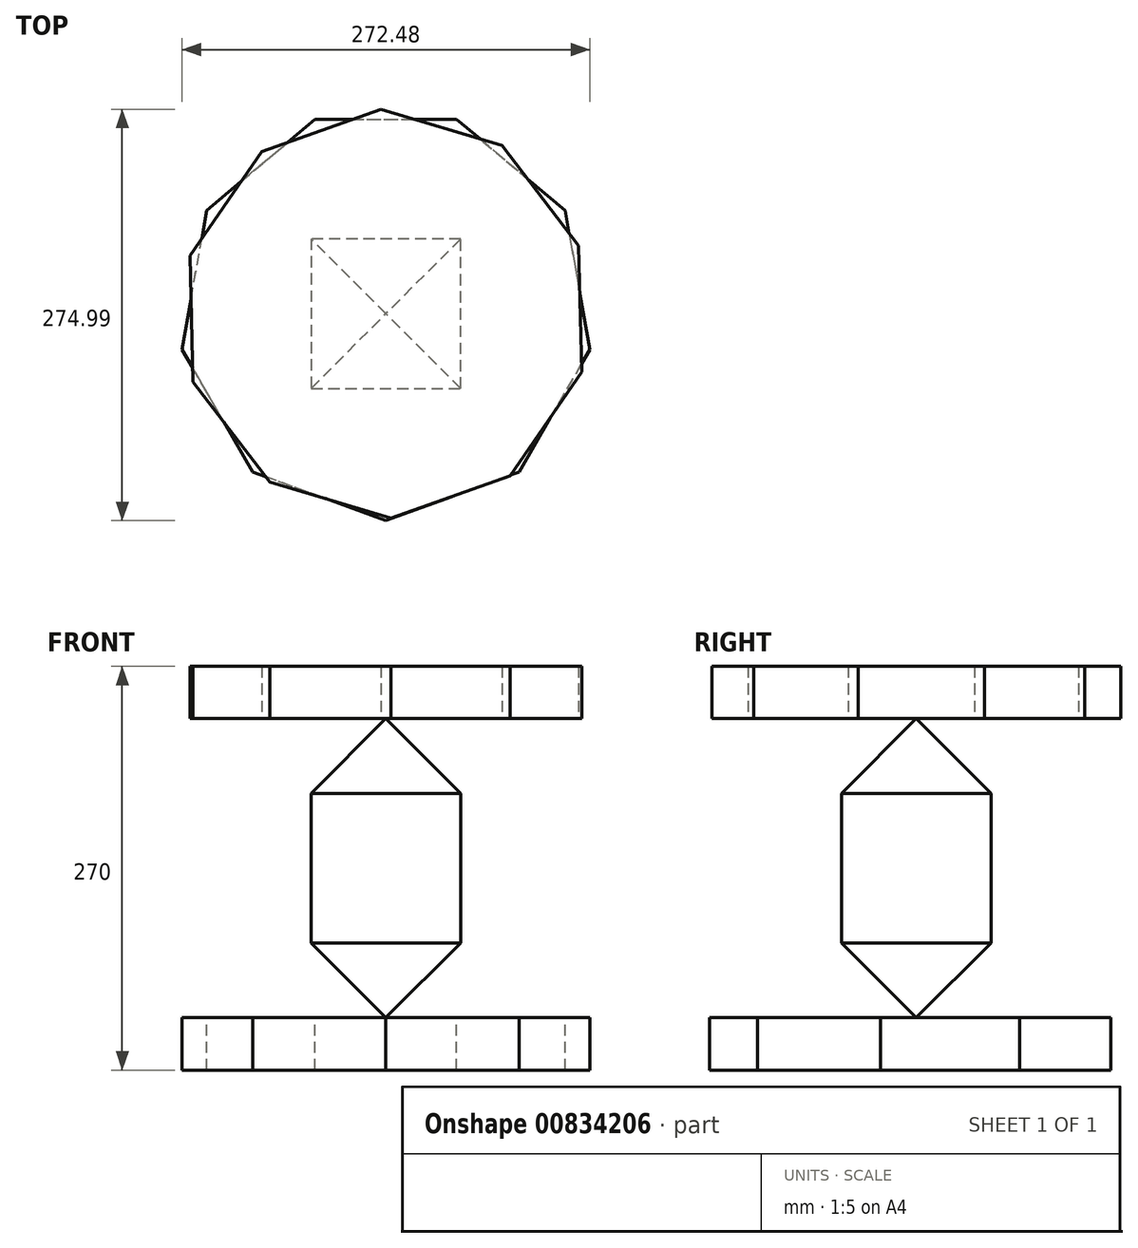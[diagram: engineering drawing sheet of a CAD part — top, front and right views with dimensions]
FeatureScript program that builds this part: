
annotation { "Feature Type Name" : "Feature", "Feature Type Description" : "" }
export const myFeature = defineFeature(function(context is Context, id is Id, definition is map)
    precondition{}
    {
        {
            var Q0;
            Q0=qCreatedBy(makeId("Top.planeOp"),FACE);
            var sketch = newSketch(context, id + "F0", { "sketchPlane" : qUnion([Q0])});
            skLineSegment(sketch, "E0.bottom", {"start": v(-50, 50) * mm, "end": v(50, 50) * mm});
            skLineSegment(sketch, "E0.top", {"start": v(-50, -50) * mm, "end": v(50, -50) * mm});
            skLineSegment(sketch, "E0.left", {"start": v(-50, 50) * mm, "end": v(-50, -50) * mm});
            skLineSegment(sketch, "E0.right", {"start": v(50, 50) * mm, "end": v(50, -50) * mm});
            skPoint(sketch, "E0.middle", {"position": v(0, 0) * mm});
            skSolve(sketch);
        }
        {
            var Q0;
            Q0=makeQuery(id+"F0.imprint","IMPRINT",FACE,{"disambiguationData":[TD([[makeQuery(id+"F0.imprint","IMPRINT",EDGE,{"derivedFrom":sQuery(id+"F0.wireOp",EDGE,"E0.bottom")}),-1.0]])]});
            extrude(context, id + "F1", {"entities" : qUnion([Q0]), "oppositeDirection" : true, "depth" : 100 * mm, "offsetDistance" : 25 * mm});
        }
        {
            var Q0;
            Q0=makeQuery(id+"F1.opExtrude","CAP_FACE",FACE,{"disambiguationData":[OSD([sQuery(id+"F0.wireOp",EDGE,"E0.bottom"),sQuery(id+"F0.wireOp",EDGE,"E0.top"),sQuery(id+"F0.wireOp",EDGE,"E0.left"),sQuery(id+"F0.wireOp",EDGE,"E0.right")])],"isStart":true});
            extrude(context, id + "F2", {"entities" : qUnion([Q0]), "operationType" : NewBodyOperationType.ADD, "depth" : 50 * mm, "offsetDistance" : 25 * mm});
        }
        {
            var Q0;
            Q0=makeQuery(id+"F2.opExtrude","CAP_EDGE",EDGE,{"disambiguationData":[OSD([sQuery(id+"F0.wireOp",EDGE,"E0.top")])],"isStart":false});
            var Q1;
            Q1=makeQuery(id+"F2.opExtrude","CAP_EDGE",EDGE,{"disambiguationData":[OSD([sQuery(id+"F0.wireOp",EDGE,"E0.bottom")])],"isStart":false});
            var Q2;
            Q2=makeQuery(id+"F2.opExtrude","CAP_EDGE",EDGE,{"disambiguationData":[OSD([sQuery(id+"F0.wireOp",EDGE,"E0.right")])],"isStart":false});
            var Q3;
            Q3=makeQuery(id+"F2.opExtrude","CAP_EDGE",EDGE,{"disambiguationData":[OSD([sQuery(id+"F0.wireOp",EDGE,"E0.left")])],"isStart":false});
            chamfer(context, id + "F3", {"entities" : qUnion([Q0, Q1, Q2, Q3]), "width" : 50 * mm, "tangentPropagation" : true});
        }
        {
            var Q0;
            Q0=qCreatedBy(makeId("Top.planeOp"),FACE);
            cPlane(context, id + "F4", {"entities" : qUnion([Q0]), "cplaneType" : CPlaneType.OFFSET, "offset" : 50 * mm, "width" : 150 * mm, "height" : 150 * mm});
        }
        {
            var Q0;
            Q0=qCreatedBy(id+"F4.planeOp",FACE);
            var sketch = newSketch(context, id + "F5", { "sketchPlane" : qUnion([Q0])});
            skCircle(sketch, "E1.cCircle", {"center": v(0, 0) * mm, "radius": 130 * mm, "construction": true});
            skLineSegment(sketch, "E1.0", {"start": v(131.02, -38.96) * mm, "end": v(83.1, -108.53) * mm});
            skLineSegment(sketch, "E1.1", {"start": v(83.1, -108.53) * mm, "end": v(3.44, -136.65) * mm});
            skLineSegment(sketch, "E1.2", {"start": v(3.44, -136.65) * mm, "end": v(-77.54, -112.57) * mm});
            skLineSegment(sketch, "E1.3", {"start": v(-77.54, -112.57) * mm, "end": v(-128.9, -45.5) * mm});
            skLineSegment(sketch, "E1.4", {"start": v(-128.9, -45.5) * mm, "end": v(-131.02, 38.96) * mm});
            skLineSegment(sketch, "E1.5", {"start": v(-131.02, 38.96) * mm, "end": v(-83.1, 108.53) * mm});
            skLineSegment(sketch, "E1.6", {"start": v(-83.1, 108.53) * mm, "end": v(-3.44, 136.65) * mm});
            skLineSegment(sketch, "E1.7", {"start": v(-3.44, 136.65) * mm, "end": v(77.54, 112.57) * mm});
            skLineSegment(sketch, "E1.8", {"start": v(77.54, 112.57) * mm, "end": v(128.9, 45.5) * mm});
            skLineSegment(sketch, "E1.9", {"start": v(128.9, 45.5) * mm, "end": v(131.02, -38.96) * mm});
            skPoint(sketch, "E1.0.midPoint", {"position": v(107.06, -73.74) * mm});
            skSolve(sketch);
        }
        {
            var Q0;
            Q0=makeQuery(id+"F5.imprint","IMPRINT",FACE,{"disambiguationData":[TD([[makeQuery(id+"F5.imprint","IMPRINT",EDGE,{"derivedFrom":sQuery(id+"F5.wireOp",EDGE,"E1.0")}),-1.0]])]});
            extrude(context, id + "F6", {"entities" : qUnion([Q0]), "operationType" : NewBodyOperationType.ADD, "depth" : 35 * mm, "offsetDistance" : 25 * mm});
        }
        {
            var Q0;
            Q0=makeQuery(id+"F1.opExtrude","CAP_FACE",FACE,{"disambiguationData":[OSD([sQuery(id+"F0.wireOp",EDGE,"E0.bottom"),sQuery(id+"F0.wireOp",EDGE,"E0.top"),sQuery(id+"F0.wireOp",EDGE,"E0.left"),sQuery(id+"F0.wireOp",EDGE,"E0.right")])],"isStart":false});
            extrude(context, id + "F7", {"entities" : qUnion([Q0]), "operationType" : NewBodyOperationType.ADD, "depth" : 50 * mm, "offsetDistance" : 25 * mm});
        }
        {
            var Q0;
            Q0=makeQuery(id+"F7.opExtrude","CAP_EDGE",EDGE,{"disambiguationData":[OSD([sQuery(id+"F0.wireOp",EDGE,"E0.top")])],"isStart":false});
            var Q1;
            Q1=makeQuery(id+"F7.opExtrude","CAP_EDGE",EDGE,{"disambiguationData":[OSD([sQuery(id+"F0.wireOp",EDGE,"E0.right")])],"isStart":false});
            var Q2;
            Q2=makeQuery(id+"F7.opExtrude","CAP_EDGE",EDGE,{"disambiguationData":[OSD([sQuery(id+"F0.wireOp",EDGE,"E0.left")])],"isStart":false});
            var Q3;
            Q3=makeQuery(id+"F7.opExtrude","CAP_EDGE",EDGE,{"disambiguationData":[OSD([sQuery(id+"F0.wireOp",EDGE,"E0.bottom")])],"isStart":false});
            chamfer(context, id + "F8", {"entities" : qUnion([Q0, Q1, Q2, Q3]), "width" : 50 * mm, "tangentPropagation" : true});
        }
        {
            var Q0;
            Q0=qCreatedBy(makeId("Top.planeOp"),FACE);
            cPlane(context, id + "F9", {"entities" : qUnion([Q0]), "cplaneType" : CPlaneType.OFFSET, "offset" : 150 * mm, "oppositeDirection" : true, "width" : 150 * mm, "height" : 150 * mm});
        }
        {
            var Q0;
            Q0=qCreatedBy(id+"F9.planeOp",FACE);
            var sketch = newSketch(context, id + "F10", { "sketchPlane" : qUnion([Q0])});
            skCircle(sketch, "E2.cCircle", {"center": v(0, 0) * mm, "radius": 130 * mm, "construction": true});
            skLineSegment(sketch, "E2.0", {"start": v(-47.32, 130) * mm, "end": v(47.32, 130) * mm});
            skLineSegment(sketch, "E2.1", {"start": v(47.32, 130) * mm, "end": v(119.8, 69.17) * mm});
            skLineSegment(sketch, "E2.2", {"start": v(119.8, 69.17) * mm, "end": v(136.24, -24.02) * mm});
            skLineSegment(sketch, "E2.3", {"start": v(136.24, -24.02) * mm, "end": v(88.93, -105.98) * mm});
            skLineSegment(sketch, "E2.4", {"start": v(88.93, -105.98) * mm, "end": v(0, -138.34) * mm});
            skLineSegment(sketch, "E2.5", {"start": v(0, -138.34) * mm, "end": v(-88.93, -105.98) * mm});
            skLineSegment(sketch, "E2.6", {"start": v(-88.93, -105.98) * mm, "end": v(-136.24, -24.02) * mm});
            skLineSegment(sketch, "E2.7", {"start": v(-136.24, -24.02) * mm, "end": v(-119.8, 69.17) * mm});
            skLineSegment(sketch, "E2.8", {"start": v(-119.8, 69.17) * mm, "end": v(-47.32, 130) * mm});
            skPoint(sketch, "E2.0.midPoint", {"position": v(0, 130) * mm});
            skSolve(sketch);
        }
        {
            var Q0;
            Q0=makeQuery(id+"F10.imprint","IMPRINT",FACE,{"disambiguationData":[TD([[makeQuery(id+"F10.imprint","IMPRINT",EDGE,{"derivedFrom":sQuery(id+"F10.wireOp",EDGE,"E2.0")}),-1.0]])]});
            extrude(context, id + "F11", {"entities" : qUnion([Q0]), "operationType" : NewBodyOperationType.ADD, "oppositeDirection" : true, "depth" : 35 * mm, "offsetDistance" : 25 * mm});
        }
    });
